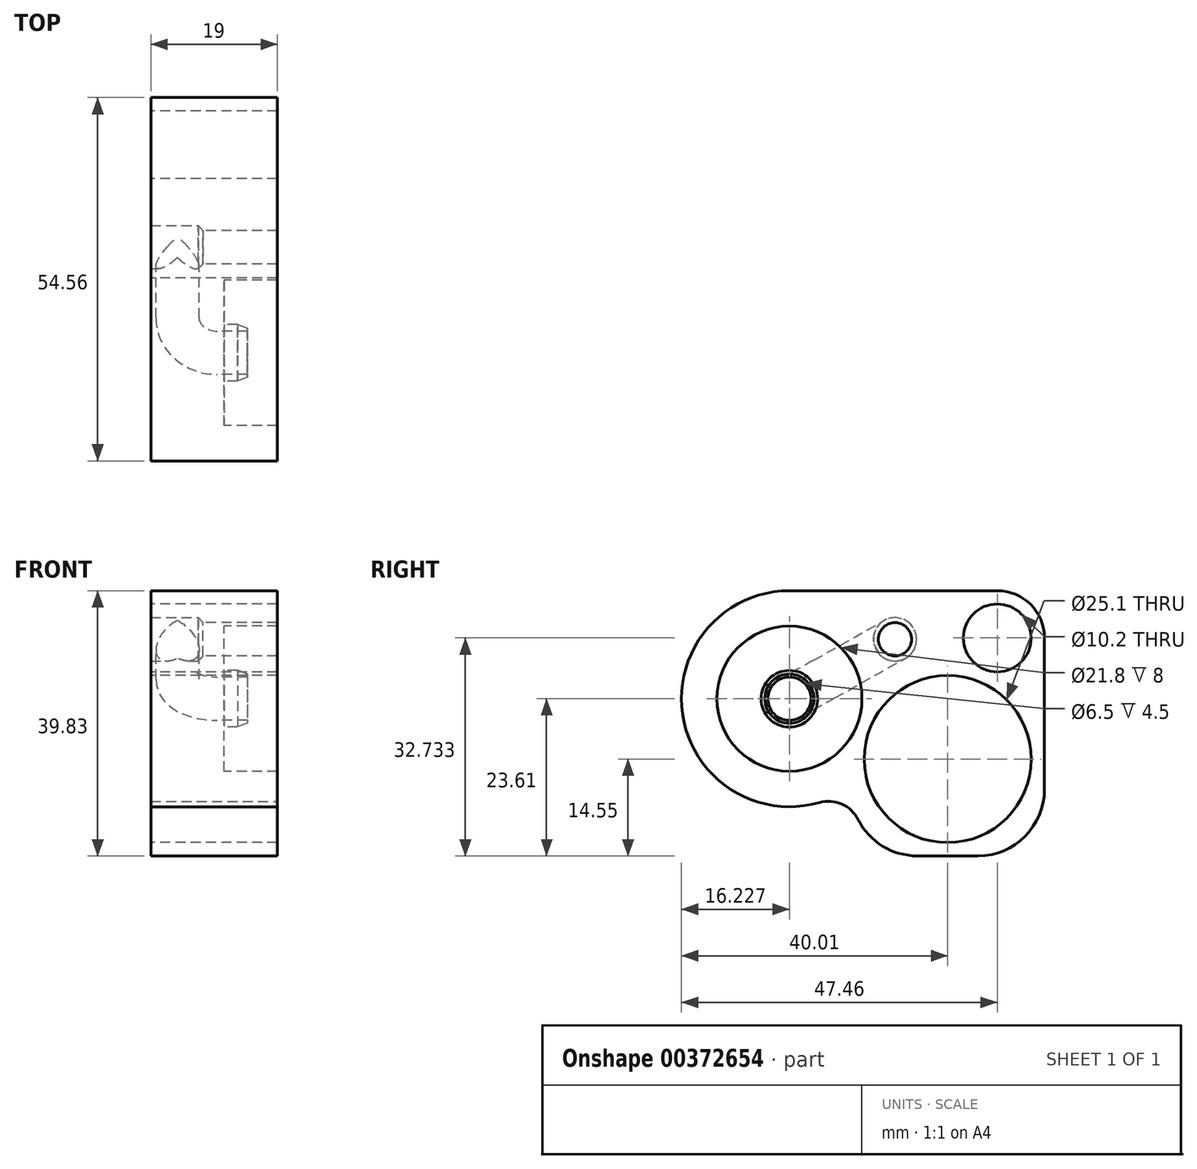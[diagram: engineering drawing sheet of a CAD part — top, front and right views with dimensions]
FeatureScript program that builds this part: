
annotation { "Feature Type Name" : "Feature", "Feature Type Description" : "" }
export const myFeature = defineFeature(function(context is Context, id is Id, definition is map)
    precondition{}
    {
        {
            var Q0;
            Q0=qCreatedBy(makeId("Right.planeOp"),FACE);
            var sketch = newSketch(context, id + "F0", { "sketchPlane" : qUnion([Q0])});
            skCircle(sketch, "E0", {"center": v(0, 0) * mm, "radius": 12.55 * mm});
            skCircle(sketch, "E1", {"center": v(-7.92, 17.98) * mm, "radius": 4.3 * mm, "construction": true});
            skCircle(sketch, "E2", {"center": v(7.45, 18.18) * mm, "radius": 5.1 * mm});
            skLineSegment(sketch, "E3", {"start": v(-7.92, 17.98) * mm, "end": v(0, 0) * mm, "construction": true});
            skLineSegment(sketch, "E4", {"start": v(7.45, 18.18) * mm, "end": v(0, 0) * mm, "construction": true});
            skCircle(sketch, "E5", {"center": v(-23.78, 9.06) * mm, "radius": 10.9 * mm});
            skLineSegment(sketch, "E6", {"start": v(-23.78, 9.06) * mm, "end": v(0, 0) * mm, "construction": true});
            skArc(sketch, "E7", {"start": v(-23.78, 25.28) * mm, "mid": v(-39.27, 4.22) * mm, "end": v(-14.55, -4.28) * mm});
            skArc(sketch, "E8", {"start": v(14.55, 18.18) * mm, "mid": v(12.47, 23.2) * mm, "end": v(7.45, 25.28) * mm});
            skLineSegment(sketch, "E9", {"start": v(7.45, 25.28) * mm, "end": v(-23.78, 25.28) * mm});
            skLineSegment(sketch, "E10", {"start": v(14.55, 18.18) * mm, "end": v(14.55, -14.55) * mm});
            skPoint(sketch, "E10.endSnap0", {"position": v(14.55, 18.18) * mm});
            skLineSegment(sketch, "E11", {"start": v(-14.55, -4.28) * mm, "end": v(-14.55, -14.55) * mm});
            skLineSegment(sketch, "E12", {"start": v(-14.55, -14.55) * mm, "end": v(14.55, -14.55) * mm});
            skCircle(sketch, "E13", {"center": v(-7.92, 17.98) * mm, "radius": 2.5 * mm});
            skLineSegment(sketch, "E14", {"start": v(-7.92, 17.98) * mm, "end": v(-23.78, 9.06) * mm, "construction": true});
            skCircle(sketch, "E15", {"center": v(-7.92, 17.98) * mm, "radius": 3.25 * mm});
            skSolve(sketch);
        }
        {
            var Q0;
            Q0=qSketchRegion(id+"F0",true);
            var Q1;
            Q1=makeQuery(id+"F0.imprint","IMPRINT",FACE,{"disambiguationData":[TD([[makeQuery(id+"F0.imprint","IMPRINT",EDGE,{"derivedFrom":sQuery(id+"F0.wireOp",EDGE,"E13")}),-1.0]])]});
            extrude(context, id + "F1", {"entities" : qUnion([Q0, Q1]), "depth" : 9 * mm, "offsetDistance" : 25 * mm});
        }
        {
            var Q0;
            Q0=makeQuery(id+"F0.imprint","IMPRINT",FACE,{"disambiguationData":[TD([[makeQuery(id+"F0.imprint","IMPRINT",EDGE,{"derivedFrom":sQuery(id+"F0.wireOp",EDGE,"E0")}),-1.0]])]});
            var Q1;
            Q1=makeQuery(id+"F0.imprint","IMPRINT",FACE,{"disambiguationData":[TD([[makeQuery(id+"F0.imprint","IMPRINT",EDGE,{"derivedFrom":sQuery(id+"F0.wireOp",EDGE,"E5")}),1.0]])]});
            extrude(context, id + "F2", {"entities" : qUnion([Q0, Q1]), "operationType" : NewBodyOperationType.ADD, "oppositeDirection" : true, "depth" : 10 * mm, "offsetDistance" : 25 * mm});
        }
        {
            var Q0;
            Q0=makeQuery(id+"F1.opExtrude","SWEPT_EDGE",EDGE,{"disambiguationData":[OSD([sQuery(id+"F0.wireOp",EDGE,"E7"),sQuery(id+"F0.wireOp",EDGE,"E9")])]});
            var Q1;
            Q1=makeQuery(id+"F1.opExtrude","SWEPT_EDGE",EDGE,{"disambiguationData":[OSD([sQuery(id+"F0.wireOp",EDGE,"E8"),sQuery(id+"F0.wireOp",EDGE,"E10")])]});
            var Q2;
            Q2=makeQuery(id+"F1.opExtrude","SWEPT_EDGE",EDGE,{"disambiguationData":[OSD([sQuery(id+"F0.wireOp",EDGE,"E8"),sQuery(id+"F0.wireOp",EDGE,"E9")])]});
            var Q3;
            Q3=makeQuery(id+"F1.opExtrude","SWEPT_EDGE",EDGE,{"disambiguationData":[OSD([sQuery(id+"F0.wireOp",EDGE,"E11"),sQuery(id+"F0.wireOp",EDGE,"E12")])]});
            var Q4;
            Q4=makeQuery(id+"F1.opExtrude","SWEPT_EDGE",EDGE,{"disambiguationData":[OSD([sQuery(id+"F0.wireOp",EDGE,"E10"),sQuery(id+"F0.wireOp",EDGE,"E12")])]});
            fillet(context, id + "F3", {"entities" : qUnion([Q0, Q1, Q2, Q3, Q4]), "radius" : 10 * mm, "tangentPropagation" : true, "allowEdgeOverflow" : false});
        }
        {
            var Q0;
            Q0=makeQuery(id+"F1.opExtrude","SWEPT_EDGE",EDGE,{"disambiguationData":[OSD([sQuery(id+"F0.wireOp",EDGE,"E7"),sQuery(id+"F0.wireOp",EDGE,"E11")])]});
            fillet(context, id + "F4", {"entities" : qUnion([Q0]), "radius" : 5 * mm, "tangentPropagation" : true, "allowEdgeOverflow" : false});
        }
        {
            var Q0;
            Q0=qCreatedBy(makeId("Top.planeOp"),FACE);
            var Q1;
            Q1=sQuery(id+"F0.wireOp",VERTEX,"E6.start");
            cPlane(context, id + "F5", {"entities" : qUnion([Q0, Q1]), "cplaneType" : CPlaneType.PLANE_POINT, "offset" : 25 * mm, "width" : 150 * mm, "height" : 150 * mm});
        }
        {
            var Q0;
            Q0=sQuery(id+"F0.wireOp",EDGE,"E14");
            var Q1;
            Q1=qCreatedBy(id+"F5.planeOp",FACE);
            cPlane(context, id + "F6", {"entities" : qUnion([Q0, Q1]), "cplaneType" : CPlaneType.LINE_ANGLE, "offset" : 25 * mm, "angle" : 0 * degree, "width" : 150 * mm, "height" : 150 * mm});
        }
        {
            var Q0;
            Q0=qCreatedBy(id+"F5.planeOp",FACE);
            var sketch = newSketch(context, id + "F7", { "sketchPlane" : qUnion([Q0])});
            skLineSegment(sketch, "E16", {"start": v(0, -23.78) * mm, "end": v(9, -23.78) * mm, "construction": true});
            skLineSegment(sketch, "E17", {"start": v(0, -12.78) * mm, "end": v(1, -12.78) * mm});
            skLineSegment(sketch, "E18", {"start": v(1, -12.78) * mm, "end": v(1, -19.53) * mm});
            skLineSegment(sketch, "E19", {"start": v(1, -19.53) * mm, "end": v(3, -19.53) * mm});
            skLineSegment(sketch, "E20", {"start": v(3, -19.53) * mm, "end": v(4.5, -20.08) * mm});
            skLineSegment(sketch, "E21", {"start": v(4.5, -20.08) * mm, "end": v(4.5, -20.53) * mm});
            skLineSegment(sketch, "E22", {"start": v(4.5, -20.53) * mm, "end": v(0, -20.53) * mm});
            skLineSegment(sketch, "E23", {"start": v(0, -20.53) * mm, "end": v(0, -12.78) * mm});
            skSolve(sketch);
        }
        {
            var Q0;
            Q0 = qSketchRegion(id + "F7", true);
            var Q1;
            Q1=sQuery(id+"F7.wireOp",EDGE,"E16");
            revolve(context, id + "F8", {"operationType" : NewBodyOperationType.ADD, "surfaceOperationType" : NewSurfaceOperationType.NEW, "entities" : qUnion([Q0]), "axis" : qUnion([Q1]), "revolveType" : RevolveType.FULL});
        }
        {
            var Q0;
            Q0=qCreatedBy(id+"F6.planeOp",FACE);
            var sketch = newSketch(context, id + "F9", { "sketchPlane" : qUnion([Q0])});
            skLineSegment(sketch, "E24", {"start": v(-6, -1.91) * mm, "end": v(-6, 10.29) * mm});
            skArc(sketch, "E25", {"start": v(0, 16.29) * mm, "mid": v(-4.24, 14.53) * mm, "end": v(-6, 10.29) * mm});
            skLineSegment(sketch, "E26", {"start": v(0, 16.29) * mm, "end": v(-6, 16.29) * mm, "construction": true});
            skSolve(sketch);
        }
        {
            var Q0;
            Q0=makeQuery(id+"F0.imprint","IMPRINT",FACE,{"disambiguationData":[TD([[makeQuery(id+"F0.imprint","IMPRINT",EDGE,{"derivedFrom":sQuery(id+"F0.wireOp",EDGE,"E5")}),1.0]])]});
            var sketch = newSketch(context, id + "F10", { "sketchPlane" : qUnion([Q0])});
            skCircle(sketch, "E27.0", {"center": v(-23.78, 9.06) * mm, "radius": 3.25 * mm});
            skCircle(sketch, "E28", {"center": v(-7.92, 17.98) * mm, "radius": 3.25 * mm});
            skSolve(sketch);
        }
        {
            var Q0;
            Q0=makeQuery(id+"F0.imprint","IMPRINT",FACE,{"disambiguationData":[TD([[makeQuery(id+"F0.imprint","IMPRINT",EDGE,{"derivedFrom":sQuery(id+"F0.wireOp",EDGE,"E13")}),-1.0]])]});
            extrude(context, id + "F11", {"entities" : qUnion([Q0]), "operationType" : NewBodyOperationType.ADD, "oppositeDirection" : true, "depth" : 2.9 * mm, "offsetDistance" : 25 * mm});
        }
        {
            var Q0;
            Q0=makeQuery(id+"F10.imprint","IMPRINT",FACE,{"disambiguationData":[TD([[makeQuery(id+"F10.imprint","IMPRINT",EDGE,{"derivedFrom":sQuery(id+"F10.wireOp",EDGE,"E27.0")}),1.0]])]});
            var Q1;
            Q1=sQuery(id+"F9.wireOp",EDGE,"E25");
            var Q2;
            Q2=sQuery(id+"F9.wireOp",EDGE,"E24");
            sweep(context, id + "F12", {"operationType" : NewBodyOperationType.REMOVE, "profiles" : qUnion([Q0]), "path" : qUnion([Q1, Q2])});
        }
        {
            var Q0;
            Q0=makeQuery(id+"F11.opExtrude","CAP_EDGE",EDGE,{"disambiguationData":[OSD([sQuery(id+"F0.wireOp",EDGE,"E13")])],"isStart":false});
            chamfer(context, id + "F13", {"entities" : qUnion([Q0]), "width" : 0.75 * mm, "tangentPropagation" : true});
        }
    });
